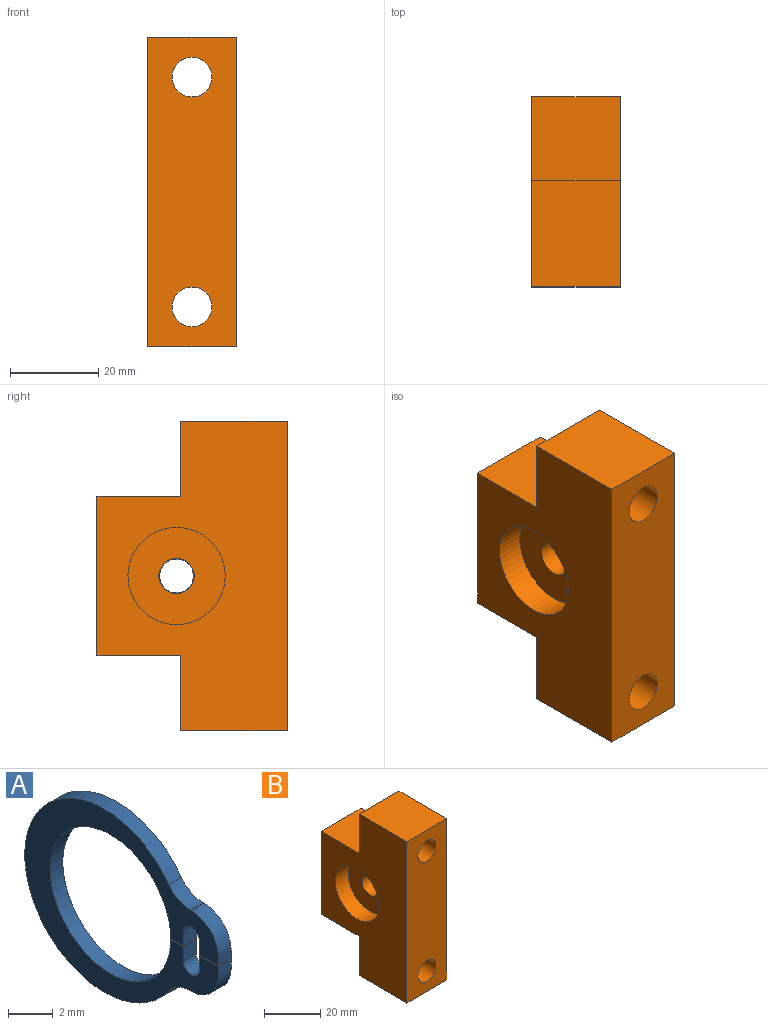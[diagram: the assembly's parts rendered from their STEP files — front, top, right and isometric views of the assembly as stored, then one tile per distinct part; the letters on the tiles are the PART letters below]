
ASSEMBLY  parts=2 mates=1
PART A: 22 faces, bbox 0.8x12.2x10 mm
  f0: cylinder r=1.7mm len=1.38mm, axis (-1,0,0), area 1.3mm2, adj f1,f16,f18,f19
  f1: cylinder r=5mm len=10mm, axis (-1,0,0), area 20.2mm2, adj f0,f16,f19,f21
  f2: plane 0.8x0.48mm, normal (0,-1,0), area 0.4mm2, adj f3,f16,f17,f19
  f3: plane 1.2x0.8mm, normal (0,0,1), area 1mm2, adj f2,f4,f16,f19
  f4: plane 0.8x0.78mm, normal (0,1,0), area 0.6mm2, adj f3,f5,f16,f19
  f5: cylinder r=0.5mm len=1mm, axis (-1,0,0), area 1.3mm2, adj f4,f6,f16,f19
  f6: plane 0.8x0.78mm, normal (0,-1,0), area 0.6mm2, adj f5,f7,f16,f19
  f7: plane 0.8x0.8mm, normal (0,0,1), area 0.6mm2, adj f6,f8,f16,f19
  f8: cylinder r=3.8mm len=7.6mm, axis (-1,0,0), area 19.1mm2, adj f7,f9,f16,f19
  f9: plane 0.8x0.8mm, normal (0,0,-1), area 0.6mm2, adj f8,f10,f16,f19
  f10: plane 0.8x0.78mm, normal (0,-1,0), area 0.6mm2, adj f9,f11,f16,f19
  f11: cylinder r=0.5mm len=1mm, axis (-1,0,0), area 1.3mm2, adj f10,f12,f16,f19
  f12: plane 0.8x0.78mm, normal (0,1,0), area 0.6mm2, adj f11,f13,f16,f19
  f13: plane 1.2x0.8mm, normal (0,0,-1), area 1mm2, adj f12,f14,f16,f19
  f14: plane 0.8x0.48mm, normal (0,-1,0), area 0.4mm2, adj f13,f15,f16,f19
  f15: cylinder r=1.7mm len=1.7mm, axis (-1,0,0), area 2.1mm2, adj f14,f16,f19,f20
  f16: plane 12.2x10mm, normal (-1,0,0), area 40.1mm2, adj f0,f1,f2,f3,f4,f5,f6,f7
  f17: cylinder r=1.7mm len=1.7mm, axis (-1,0,0), area 2.1mm2, adj f2,f16,f18,f19
  f18: plane 0.8x0.05mm, normal (0,0,-1), area 0mm2, adj f0,f16,f17,f19
  f19: plane 12.2x10mm, normal (1,0,0), area 40.1mm2, adj f0,f1,f2,f3,f4,f5,f6,f7
  f20: plane 0.8x0.05mm, normal (0,0,1), area 0mm2, adj f15,f16,f19,f21
  f21: cylinder r=1.7mm len=1.38mm, axis (-1,0,0), area 1.3mm2, adj f1,f16,f19,f20
PART B: 17 faces, bbox 20x43x70 mm
  f0: plane 20x19mm, normal (0,0,1), area 380mm2, adj f1,f4,f9,f10
  f1: plane 36x20mm, normal (0,1,0), area 720mm2, adj f0,f4,f10,f15
  f2: plane 70x20mm, normal (0,-1,0), area 1272.8mm2, adj f3,f4,f7,f10,f12,f16
  f3: plane 24x20mm, normal (0,0,1), area 480mm2, adj f2,f4,f9,f10
  f4: plane 70x43mm, normal (1,0,0), area 1983.9mm2, adj f0,f1,f2,f3,f5,f9,f11,f12
  f5: cylinder r=11mm len=22mm, axis (1,0,0), area 449.2mm2, adj f4,f6
  f6: plane 22x22mm, normal (1,0,0), area 329.9mm2, adj f5,f13
  f7: cylinder r=4.5mm len=24mm, axis (0,-1,0), area 678.6mm2, adj f2,f11
  f8: cylinder r=11mm len=22mm, axis (1,0,0), area 449.2mm2, adj f10,f14
  f9: plane 20x17mm, normal (0,1,0), area 276.4mm2, adj f0,f3,f4,f10,f16
  f10: plane 70x43mm, normal (-1,0,0), area 1983.9mm2, adj f0,f1,f2,f3,f8,f9,f11,f12
  f11: plane 20x17mm, normal (0,1,0), area 276.4mm2, adj f4,f7,f10,f12,f15
  f12: plane 24x20mm, normal (0,0,-1), area 480mm2, adj f2,f4,f10,f11
  f13: cylinder r=4mm len=8mm, axis (1,0,0), area 175.9mm2, adj f6,f14
  f14: plane 22x22mm, normal (-1,0,0), area 329.9mm2, adj f8,f13
  f15: plane 20x19mm, normal (0,0,-1), area 380mm2, adj f1,f4,f10,f11
  f16: cylinder r=4.5mm len=24mm, axis (0,1,0), area 678.6mm2, adj f2,f9
PLACE A t=(48.47,-4.26,-49.43)mm
PLACE B t=(44.57,-29.26,-49.43)mm
MATE revolute B.f5 <-> A.f8  axis (1,0,0) through (48.07,-4.26,-49.43)mm
